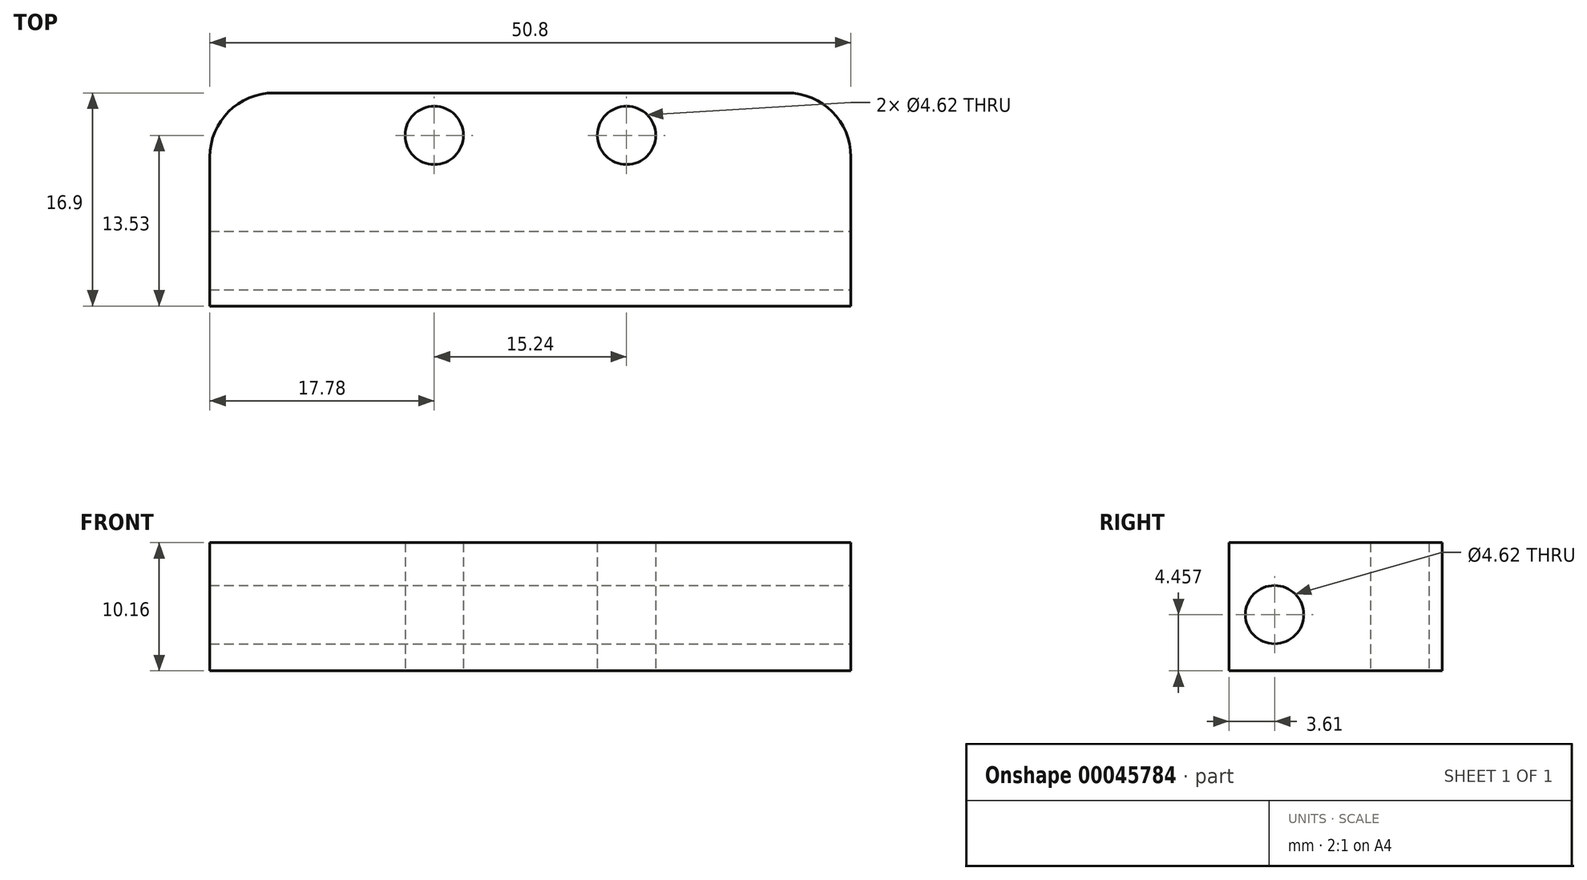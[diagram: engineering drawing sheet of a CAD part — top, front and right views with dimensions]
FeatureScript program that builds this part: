
annotation { "Feature Type Name" : "Feature", "Feature Type Description" : "" }
export const myFeature = defineFeature(function(context is Context, id is Id, definition is map)
    precondition{}
    {
        {
            var Q0;
            Q0=qCreatedBy(makeId("Top.planeOp"),FACE);
            var sketch = newSketch(context, id + "F0", { "sketchPlane" : qUnion([Q0])});
            skCircle(sketch, "E0", {"center": v(7.62, 0) * mm, "radius": 2.31 * mm});
            skCircle(sketch, "E1", {"center": v(-7.62, 0) * mm, "radius": 2.31 * mm});
            skLineSegment(sketch, "E2.bottom", {"start": v(25.4, -3.37) * mm, "end": v(-25.4, -3.37) * mm});
            skLineSegment(sketch, "E2.top", {"start": v(25.4, 3.37) * mm, "end": v(-25.4, 3.37) * mm});
            skLineSegment(sketch, "E2.left", {"start": v(25.4, -3.37) * mm, "end": v(25.4, 3.37) * mm});
            skLineSegment(sketch, "E2.right", {"start": v(-25.4, -3.37) * mm, "end": v(-25.4, 3.37) * mm});
            skPoint(sketch, "E2.middle", {"position": v(0, 0) * mm});
            skSolve(sketch);
        }
        {
            var Q0;
            Q0 = qSketchRegion(id + "F0", true);
            extrude(context, id + "F1", {"entities" : qUnion([Q0]), "depth" : 10.16 * mm});
        }
        {
            var Q0;
            Q0=makeQuery(id+"F1.opExtrude","SWEPT_FACE",FACE,{"disambiguationData":[OSD([sQuery(id+"F0.wireOp",EDGE,"E2.bottom")])]});
            var sketch = newSketch(context, id + "F2", { "sketchPlane" : qUnion([Q0])});
            skSolve(sketch);
        }
        {
            var Q0;
            {var subQ0=sQuery(id+"F0.wireOp",EDGE,"E2.bottom");Q0=makeQuery(id+"F2.imprint","IMPRINT",FACE,{"disambiguationData":[TD([[makeQuery(id+"F2.imprint","IMPRINT",EDGE,{"derivedFrom":makeQuery(id+"F1.opExtrude","CAP_EDGE",EDGE,{"disambiguationData":[OSD([subQ0])],"isStart":true})}),-1.0]])]});}
            var sketch = newSketch(context, id + "F3", { "sketchPlane" : qUnion([Q0])});
            skSolve(sketch);
        }
        {
            var Q0;
            {var subQ0=sQuery(id+"F0.wireOp",EDGE,"E2.bottom");Q0=makeQuery(id+"F3.imprint","IMPRINT",FACE,{"disambiguationData":[TD([[makeQuery(id+"F3.imprint","IMPRINT",EDGE,{"derivedFrom":makeQuery(id+"F2.imprint","IMPRINT",EDGE,{"derivedFrom":makeQuery(id+"F1.opExtrude","CAP_EDGE",EDGE,{"disambiguationData":[OSD([subQ0])],"isStart":true})})}),-1.0]])]});}
            extrude(context, id + "F4", {"entities" : qUnion([Q0]), "operationType" : NewBodyOperationType.ADD, "depth" : 10.16 * mm});
        }
        {
            var Q0;
            {var subQ0=sQuery(id+"F0.wireOp",EDGE,"E2.left");Q0=makeQuery(id+"F4.boolean.opBoolean","MERGE",FACE,{"derivedFrom":[makeQuery(id+"F1.opExtrude","SWEPT_FACE",FACE,{"disambiguationData":[OSD([subQ0])]}),makeQuery(id+"F4.opExtrude","SWEPT_FACE",FACE,{"disambiguationData":[OSD([sQuery(id+"F0.wireOp",EDGE,"E2.bottom"),subQ0])]})]});}
            var sketch = newSketch(context, id + "F5", { "sketchPlane" : qUnion([Q0])});
            skCircle(sketch, "E3", {"center": v(-9.92, 4.46) * mm, "radius": 2.31 * mm});
            skSolve(sketch);
        }
        {
            var Q0;
            Q0 = qSketchRegion(id + "F5", true);
            extrude(context, id + "F6", {"entities" : qUnion([Q0]), "operationType" : NewBodyOperationType.REMOVE, "oppositeDirection" : true, "depth" : 70.37 * mm});
        }
        {
            var Q0;
            Q0=makeQuery(id+"F1.opExtrude","SWEPT_EDGE",EDGE,{"disambiguationData":[OSD([sQuery(id+"F0.wireOp",EDGE,"E2.top"),sQuery(id+"F0.wireOp",EDGE,"E2.right")])]});
            var Q1;
            Q1=makeQuery(id+"F1.opExtrude","SWEPT_EDGE",EDGE,{"disambiguationData":[OSD([sQuery(id+"F0.wireOp",EDGE,"E2.top"),sQuery(id+"F0.wireOp",EDGE,"E2.left")])]});
            fillet(context, id + "F7", {"entities" : qUnion([Q0, Q1]), "radius" : 5.08 * mm, "tangentPropagation" : true, "allowEdgeOverflow" : false});
        }
    });
